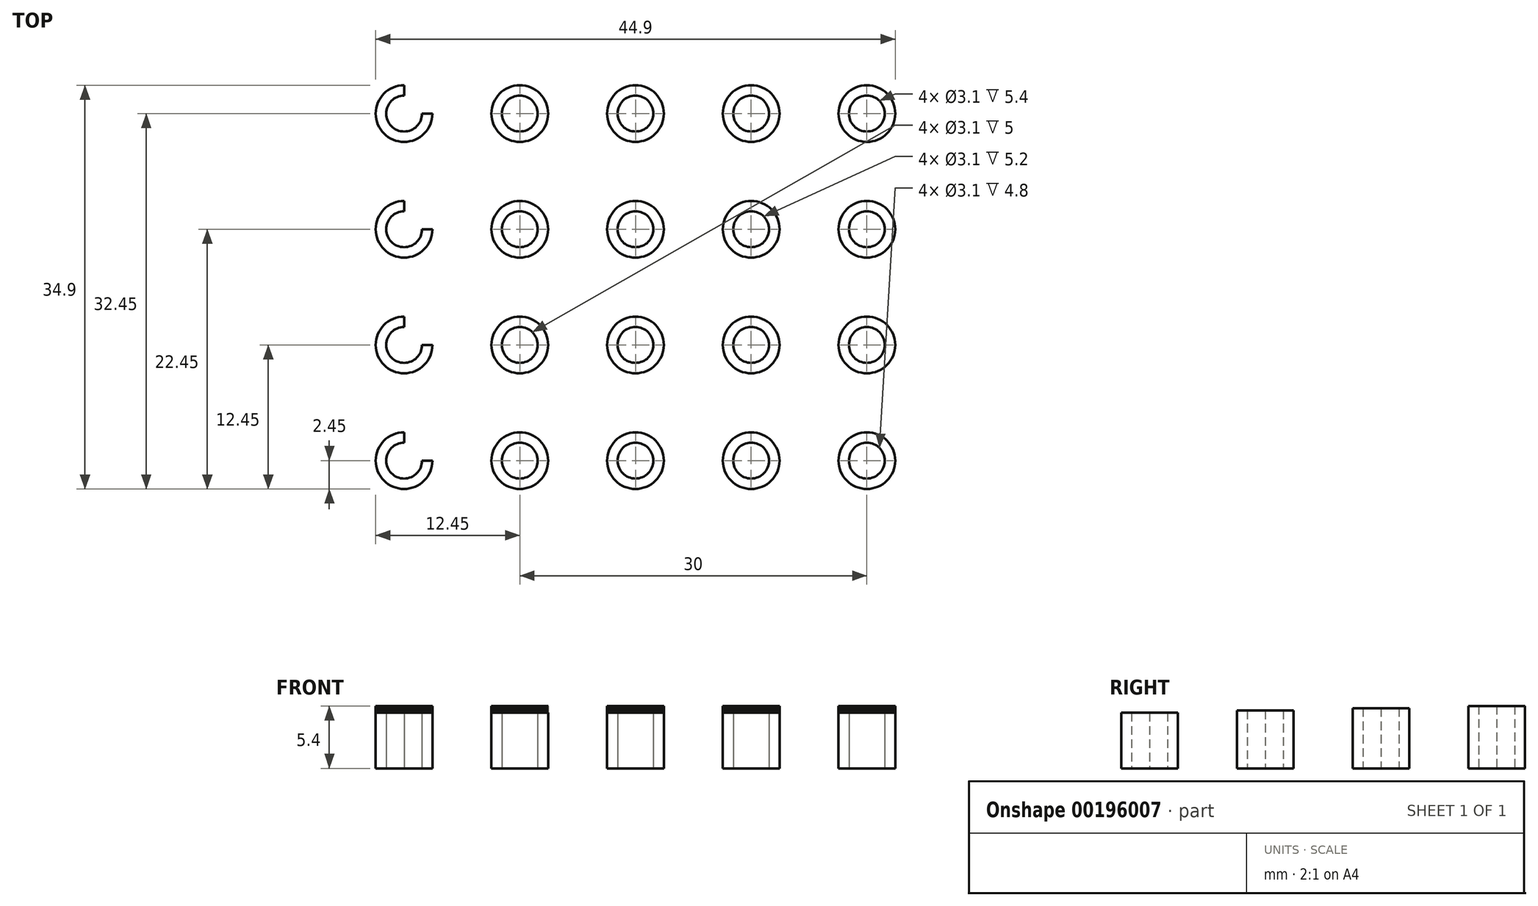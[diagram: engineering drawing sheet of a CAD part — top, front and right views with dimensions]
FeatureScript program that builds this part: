
annotation { "Feature Type Name" : "Feature", "Feature Type Description" : "" }
export const myFeature = defineFeature(function(context is Context, id is Id, definition is map)
    precondition{}
    {
        {
            var Q0;
            Q0=qCreatedBy(makeId("Top.planeOp"),FACE);
            var sketch = newSketch(context, id + "F0", { "sketchPlane" : qUnion([Q0])});
            skCircle(sketch, "E0", {"center": v(0, 0) * mm, "radius": 2.45 * mm});
            skCircle(sketch, "E1.0.1.0", {"center": v(0, 10) * mm, "radius": 2.45 * mm});
            skCircle(sketch, "E1.0.2.0", {"center": v(0, 20) * mm, "radius": 2.45 * mm});
            skCircle(sketch, "E1.0.3.0", {"center": v(0, 30) * mm, "radius": 2.45 * mm});
            skCircle(sketch, "E1.1.0.0", {"center": v(10, 0) * mm, "radius": 2.45 * mm});
            skCircle(sketch, "E1.1.1.0", {"center": v(10, 10) * mm, "radius": 2.45 * mm});
            skCircle(sketch, "E1.1.2.0", {"center": v(10, 20) * mm, "radius": 2.45 * mm});
            skCircle(sketch, "E1.1.3.0", {"center": v(10, 30) * mm, "radius": 2.45 * mm});
            skCircle(sketch, "E1.2.0.0", {"center": v(20, 0) * mm, "radius": 2.45 * mm});
            skCircle(sketch, "E1.2.1.0", {"center": v(20, 10) * mm, "radius": 2.45 * mm});
            skCircle(sketch, "E1.2.2.0", {"center": v(20, 20) * mm, "radius": 2.45 * mm});
            skCircle(sketch, "E1.2.3.0", {"center": v(20, 30) * mm, "radius": 2.45 * mm});
            skCircle(sketch, "E1.3.0.0", {"center": v(30, 0) * mm, "radius": 2.45 * mm});
            skCircle(sketch, "E1.3.1.0", {"center": v(30, 10) * mm, "radius": 2.45 * mm});
            skCircle(sketch, "E1.3.2.0", {"center": v(30, 20) * mm, "radius": 2.45 * mm});
            skCircle(sketch, "E1.3.3.0", {"center": v(30, 30) * mm, "radius": 2.45 * mm});
            skLineSegment(sketch, "E1.direction1", {"start": v(0, 0) * mm, "end": v(10, 0) * mm, "construction": true});
            skLineSegment(sketch, "E1.direction2", {"start": v(0, 0) * mm, "end": v(0, 10) * mm, "construction": true});
            skCircle(sketch, "E2.0.4.0", {"center": v(40, 0) * mm, "radius": 2.45 * mm});
            skCircle(sketch, "E2.0.4.1", {"center": v(40, 10) * mm, "radius": 2.45 * mm});
            skCircle(sketch, "E2.0.4.2", {"center": v(40, 20) * mm, "radius": 2.45 * mm});
            skCircle(sketch, "E2.0.4.3", {"center": v(40, 30) * mm, "radius": 2.45 * mm});
            skSolve(sketch);
        }
        {
            var Q0;
            Q0=makeQuery(id+"F0.imprint","IMPRINT",FACE,{"disambiguationData":[TD([[makeQuery(id+"F0.imprint","IMPRINT",EDGE,{"derivedFrom":sQuery(id+"F0.wireOp",EDGE,"E0")}),1.0]])]});
            var Q1;
            Q1=makeQuery(id+"F0.imprint","IMPRINT",FACE,{"disambiguationData":[TD([[makeQuery(id+"F0.imprint","IMPRINT",EDGE,{"derivedFrom":sQuery(id+"F0.wireOp",EDGE,"E1.1.0.0")}),1.0]])]});
            var Q2;
            Q2=makeQuery(id+"F0.imprint","IMPRINT",FACE,{"disambiguationData":[TD([[makeQuery(id+"F0.imprint","IMPRINT",EDGE,{"derivedFrom":sQuery(id+"F0.wireOp",EDGE,"E1.2.0.0")}),1.0]])]});
            var Q3;
            Q3=makeQuery(id+"F0.imprint","IMPRINT",FACE,{"disambiguationData":[TD([[makeQuery(id+"F0.imprint","IMPRINT",EDGE,{"derivedFrom":sQuery(id+"F0.wireOp",EDGE,"E1.3.0.0")}),1.0]])]});
            var Q4;
            Q4=makeQuery(id+"F0.imprint","IMPRINT",FACE,{"disambiguationData":[TD([[makeQuery(id+"F0.imprint","IMPRINT",EDGE,{"derivedFrom":sQuery(id+"F0.wireOp",EDGE,"E2.0.4.0")}),1.0]])]});
            extrude(context, id + "F1", {"entities" : qUnion([Q0, Q1, Q2, Q3, Q4]), "depth" : 4.8 * mm});
        }
        {
            var Q0;
            Q0=makeQuery(id+"F0.imprint","IMPRINT",FACE,{"disambiguationData":[TD([[makeQuery(id+"F0.imprint","IMPRINT",EDGE,{"derivedFrom":sQuery(id+"F0.wireOp",EDGE,"E1.0.1.0")}),1.0]])]});
            var Q1;
            Q1=makeQuery(id+"F0.imprint","IMPRINT",FACE,{"disambiguationData":[TD([[makeQuery(id+"F0.imprint","IMPRINT",EDGE,{"derivedFrom":sQuery(id+"F0.wireOp",EDGE,"E1.1.1.0")}),1.0]])]});
            var Q2;
            Q2=makeQuery(id+"F0.imprint","IMPRINT",FACE,{"disambiguationData":[TD([[makeQuery(id+"F0.imprint","IMPRINT",EDGE,{"derivedFrom":sQuery(id+"F0.wireOp",EDGE,"E1.2.1.0")}),1.0]])]});
            var Q3;
            Q3=makeQuery(id+"F0.imprint","IMPRINT",FACE,{"disambiguationData":[TD([[makeQuery(id+"F0.imprint","IMPRINT",EDGE,{"derivedFrom":sQuery(id+"F0.wireOp",EDGE,"E1.3.1.0")}),1.0]])]});
            var Q4;
            Q4=makeQuery(id+"F0.imprint","IMPRINT",FACE,{"disambiguationData":[TD([[makeQuery(id+"F0.imprint","IMPRINT",EDGE,{"derivedFrom":sQuery(id+"F0.wireOp",EDGE,"E2.0.4.1")}),1.0]])]});
            extrude(context, id + "F2", {"entities" : qUnion([Q0, Q1, Q2, Q3, Q4]), "depth" : 5 * mm});
        }
        {
            var Q0;
            Q0=makeQuery(id+"F0.imprint","IMPRINT",FACE,{"disambiguationData":[TD([[makeQuery(id+"F0.imprint","IMPRINT",EDGE,{"derivedFrom":sQuery(id+"F0.wireOp",EDGE,"E1.0.2.0")}),1.0]])]});
            var Q1;
            Q1=makeQuery(id+"F0.imprint","IMPRINT",FACE,{"disambiguationData":[TD([[makeQuery(id+"F0.imprint","IMPRINT",EDGE,{"derivedFrom":sQuery(id+"F0.wireOp",EDGE,"E1.1.2.0")}),1.0]])]});
            var Q2;
            Q2=makeQuery(id+"F0.imprint","IMPRINT",FACE,{"disambiguationData":[TD([[makeQuery(id+"F0.imprint","IMPRINT",EDGE,{"derivedFrom":sQuery(id+"F0.wireOp",EDGE,"E1.2.2.0")}),1.0]])]});
            var Q3;
            Q3=makeQuery(id+"F0.imprint","IMPRINT",FACE,{"disambiguationData":[TD([[makeQuery(id+"F0.imprint","IMPRINT",EDGE,{"derivedFrom":sQuery(id+"F0.wireOp",EDGE,"E1.3.2.0")}),1.0]])]});
            var Q4;
            Q4=makeQuery(id+"F0.imprint","IMPRINT",FACE,{"disambiguationData":[TD([[makeQuery(id+"F0.imprint","IMPRINT",EDGE,{"derivedFrom":sQuery(id+"F0.wireOp",EDGE,"E2.0.4.2")}),1.0]])]});
            extrude(context, id + "F3", {"entities" : qUnion([Q0, Q1, Q2, Q3, Q4]), "depth" : 5.2 * mm});
        }
        {
            var Q0;
            Q0=makeQuery(id+"F0.imprint","IMPRINT",FACE,{"disambiguationData":[TD([[makeQuery(id+"F0.imprint","IMPRINT",EDGE,{"derivedFrom":sQuery(id+"F0.wireOp",EDGE,"E1.0.3.0")}),1.0]])]});
            var Q1;
            Q1=makeQuery(id+"F0.imprint","IMPRINT",FACE,{"disambiguationData":[TD([[makeQuery(id+"F0.imprint","IMPRINT",EDGE,{"derivedFrom":sQuery(id+"F0.wireOp",EDGE,"E1.1.3.0")}),1.0]])]});
            var Q2;
            Q2=makeQuery(id+"F0.imprint","IMPRINT",FACE,{"disambiguationData":[TD([[makeQuery(id+"F0.imprint","IMPRINT",EDGE,{"derivedFrom":sQuery(id+"F0.wireOp",EDGE,"E1.2.3.0")}),1.0]])]});
            var Q3;
            Q3=makeQuery(id+"F0.imprint","IMPRINT",FACE,{"disambiguationData":[TD([[makeQuery(id+"F0.imprint","IMPRINT",EDGE,{"derivedFrom":sQuery(id+"F0.wireOp",EDGE,"E1.3.3.0")}),1.0]])]});
            var Q4;
            Q4=makeQuery(id+"F0.imprint","IMPRINT",FACE,{"disambiguationData":[TD([[makeQuery(id+"F0.imprint","IMPRINT",EDGE,{"derivedFrom":sQuery(id+"F0.wireOp",EDGE,"E2.0.4.3")}),1.0]])]});
            extrude(context, id + "F4", {"entities" : qUnion([Q0, Q1, Q2, Q3, Q4]), "depth" : 5.4 * mm});
        }
        {
            var Q0;
            Q0=sQuery(id+"F0.wireOp",VERTEX,"E0.center");
            var Q1;
            Q1=sQuery(id+"F0.wireOp",VERTEX,"E1.1.0.0.center");
            var Q2;
            Q2=sQuery(id+"F0.wireOp",VERTEX,"E1.2.0.0.center");
            var Q3;
            Q3=sQuery(id+"F0.wireOp",VERTEX,"E1.3.0.0.center");
            var Q4;
            Q4=sQuery(id+"F0.wireOp",VERTEX,"E1.3.1.0.center");
            var Q5;
            Q5=sQuery(id+"F0.wireOp",VERTEX,"E1.2.1.0.center");
            var Q6;
            Q6=sQuery(id+"F0.wireOp",VERTEX,"E1.1.1.0.center");
            var Q7;
            Q7=sQuery(id+"F0.wireOp",VERTEX,"E1.0.1.0.center");
            var Q8;
            Q8=sQuery(id+"F0.wireOp",VERTEX,"E1.0.2.0.center");
            var Q9;
            Q9=sQuery(id+"F0.wireOp",VERTEX,"E1.0.3.0.center");
            var Q10;
            Q10=sQuery(id+"F0.wireOp",VERTEX,"E1.1.3.0.center");
            var Q11;
            Q11=sQuery(id+"F0.wireOp",VERTEX,"E1.1.2.0.center");
            var Q12;
            Q12=sQuery(id+"F0.wireOp",VERTEX,"E1.2.3.0.center");
            var Q13;
            Q13=sQuery(id+"F0.wireOp",VERTEX,"E1.2.2.0.center");
            var Q14;
            Q14=sQuery(id+"F0.wireOp",VERTEX,"E1.3.2.0.center");
            var Q15;
            Q15=sQuery(id+"F0.wireOp",VERTEX,"E1.3.3.0.center");
            var Q16;
            Q16=sQuery(id+"F0.wireOp",VERTEX,"E2.0.4.0.center");
            var Q17;
            Q17=sQuery(id+"F0.wireOp",VERTEX,"E2.0.4.1.center");
            var Q18;
            Q18=sQuery(id+"F0.wireOp",VERTEX,"E2.0.4.2.center");
            var Q19;
            Q19=sQuery(id+"F0.wireOp",VERTEX,"E2.0.4.3.center");
            var Q20;
            Q20=makeQuery(id+"F1.opExtrude","SWEPT_BODY",BODY,{"disambiguationData":[OSD([sQuery(id+"F0.wireOp",EDGE,"E0")])]});
            var Q21;
            Q21=makeQuery(id+"F1.opExtrude","SWEPT_BODY",BODY,{"disambiguationData":[OSD([sQuery(id+"F0.wireOp",EDGE,"E1.1.0.0")])]});
            var Q22;
            Q22=makeQuery(id+"F1.opExtrude","SWEPT_BODY",BODY,{"disambiguationData":[OSD([sQuery(id+"F0.wireOp",EDGE,"E1.2.0.0")])]});
            var Q23;
            Q23=makeQuery(id+"F1.opExtrude","SWEPT_BODY",BODY,{"disambiguationData":[OSD([sQuery(id+"F0.wireOp",EDGE,"E1.3.0.0")])]});
            var Q24;
            Q24=makeQuery(id+"F2.opExtrude","SWEPT_BODY",BODY,{"disambiguationData":[OSD([sQuery(id+"F0.wireOp",EDGE,"E1.3.1.0")])]});
            var Q25;
            Q25=makeQuery(id+"F2.opExtrude","SWEPT_BODY",BODY,{"disambiguationData":[OSD([sQuery(id+"F0.wireOp",EDGE,"E1.2.1.0")])]});
            var Q26;
            Q26=makeQuery(id+"F2.opExtrude","SWEPT_BODY",BODY,{"disambiguationData":[OSD([sQuery(id+"F0.wireOp",EDGE,"E1.1.1.0")])]});
            var Q27;
            Q27=makeQuery(id+"F2.opExtrude","SWEPT_BODY",BODY,{"disambiguationData":[OSD([sQuery(id+"F0.wireOp",EDGE,"E1.0.1.0")])]});
            var Q28;
            Q28=makeQuery(id+"F3.opExtrude","SWEPT_BODY",BODY,{"disambiguationData":[OSD([sQuery(id+"F0.wireOp",EDGE,"E1.0.2.0")])]});
            var Q29;
            Q29=makeQuery(id+"F4.opExtrude","SWEPT_BODY",BODY,{"disambiguationData":[OSD([sQuery(id+"F0.wireOp",EDGE,"E1.0.3.0")])]});
            var Q30;
            Q30=makeQuery(id+"F4.opExtrude","SWEPT_BODY",BODY,{"disambiguationData":[OSD([sQuery(id+"F0.wireOp",EDGE,"E1.1.3.0")])]});
            var Q31;
            Q31=makeQuery(id+"F3.opExtrude","SWEPT_BODY",BODY,{"disambiguationData":[OSD([sQuery(id+"F0.wireOp",EDGE,"E1.1.2.0")])]});
            var Q32;
            Q32=makeQuery(id+"F4.opExtrude","SWEPT_BODY",BODY,{"disambiguationData":[OSD([sQuery(id+"F0.wireOp",EDGE,"E1.2.3.0")])]});
            var Q33;
            Q33=makeQuery(id+"F3.opExtrude","SWEPT_BODY",BODY,{"disambiguationData":[OSD([sQuery(id+"F0.wireOp",EDGE,"E1.2.2.0")])]});
            var Q34;
            Q34=makeQuery(id+"F3.opExtrude","SWEPT_BODY",BODY,{"disambiguationData":[OSD([sQuery(id+"F0.wireOp",EDGE,"E1.3.2.0")])]});
            var Q35;
            Q35=makeQuery(id+"F4.opExtrude","SWEPT_BODY",BODY,{"disambiguationData":[OSD([sQuery(id+"F0.wireOp",EDGE,"E1.3.3.0")])]});
            var Q36;
            Q36=makeQuery(id+"F1.opExtrude","SWEPT_BODY",BODY,{"disambiguationData":[OSD([sQuery(id+"F0.wireOp",EDGE,"E2.0.4.0")])]});
            var Q37;
            Q37=makeQuery(id+"F2.opExtrude","SWEPT_BODY",BODY,{"disambiguationData":[OSD([sQuery(id+"F0.wireOp",EDGE,"E2.0.4.1")])]});
            var Q38;
            Q38=makeQuery(id+"F3.opExtrude","SWEPT_BODY",BODY,{"disambiguationData":[OSD([sQuery(id+"F0.wireOp",EDGE,"E2.0.4.2")])]});
            var Q39;
            Q39=makeQuery(id+"F4.opExtrude","SWEPT_BODY",BODY,{"disambiguationData":[OSD([sQuery(id+"F0.wireOp",EDGE,"E2.0.4.3")])]});
            hole(context, id + "F5", {"style" : HoleStyle.SIMPLE, "endStyle" : HoleEndStyle.THROUGH, "oppositeDirection" : true, "holeDiameter" : 3.1 * mm, "startFromSketch" : true, "locations" : qUnion([Q0, Q1, Q2, Q3, Q4, Q5, Q6, Q7, Q8, Q9, Q10, Q11, Q12, Q13, Q14, Q15, Q16, Q17, Q18, Q19]), "scope" : qUnion([Q20, Q21, Q22, Q23, Q24, Q25, Q26, Q27, Q28, Q29, Q30, Q31, Q32, Q33, Q34, Q35, Q36, Q37, Q38, Q39]), "isTappedThrough" : true});
        }
        {
            var Q0;
            Q0=qCreatedBy(makeId("Top.planeOp"),FACE);
            var sketch = newSketch(context, id + "F6", { "sketchPlane" : qUnion([Q0])});
            skLineSegment(sketch, "E3", {"start": v(0, 2.45) * mm, "end": v(0, 0) * mm});
            skLineSegment(sketch, "E4", {"start": v(0, 0) * mm, "end": v(2.45, 0) * mm});
            skArc(sketch, "E5", {"start": v(0, 2.45) * mm, "mid": v(1.73, 1.73) * mm, "end": v(2.45, 0) * mm});
            skLineSegment(sketch, "E6.0.1.0", {"start": v(0, 12.45) * mm, "end": v(0, 10) * mm});
            skArc(sketch, "E6.0.1.1", {"start": v(0, 12.45) * mm, "mid": v(1.73, 11.73) * mm, "end": v(2.45, 10) * mm});
            skLineSegment(sketch, "E6.0.1.2", {"start": v(0, 10) * mm, "end": v(2.45, 10) * mm});
            skLineSegment(sketch, "E6.0.2.0", {"start": v(0, 22.45) * mm, "end": v(0, 20) * mm});
            skArc(sketch, "E6.0.2.1", {"start": v(0, 22.45) * mm, "mid": v(1.73, 21.73) * mm, "end": v(2.45, 20) * mm});
            skLineSegment(sketch, "E6.0.2.2", {"start": v(0, 20) * mm, "end": v(2.45, 20) * mm});
            skLineSegment(sketch, "E6.0.3.0", {"start": v(0, 32.45) * mm, "end": v(0, 30) * mm});
            skArc(sketch, "E6.0.3.1", {"start": v(0, 32.45) * mm, "mid": v(1.73, 31.73) * mm, "end": v(2.45, 30) * mm});
            skLineSegment(sketch, "E6.0.3.2", {"start": v(0, 30) * mm, "end": v(2.45, 30) * mm});
            skLineSegment(sketch, "E6.direction1", {"start": v(0, 0) * mm, "end": v(25, 0) * mm, "construction": true});
            skLineSegment(sketch, "E6.direction2", {"start": v(0, 0) * mm, "end": v(0, 10) * mm, "construction": true});
            skSolve(sketch);
        }
        {
            var Q0;
            Q0 = qSketchRegion(id + "F6", true);
            extrude(context, id + "F7", {"entities" : qUnion([Q0]), "operationType" : NewBodyOperationType.REMOVE, "endBound" : BoundingType.THROUGH_ALL, "depth" : 25 * mm});
        }
    });
